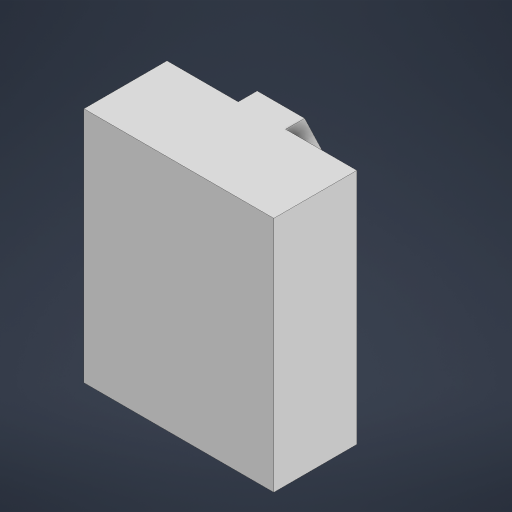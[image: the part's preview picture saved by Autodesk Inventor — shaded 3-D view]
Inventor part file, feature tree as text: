
AUTODESK INVENTOR PART (.ipt)
format: ipt  version: 2024.1 (Build 281209000, 209)  size: 168,960 bytes
history: native  units: mm
features: extrude x3, sketch x3
ambient origin geometry x8: Origin, YZ Plane, XZ Plane, XY Plane, X Axis, Y Axis, Z Axis, Center Point
bodies: Solid1 (feature_tree)
feature tree (6):
  extrude  "Extrusion1"  Depth=3.5mm
  extrude  "Extrusion2"  Depth=2.0mm
  extrude  "Extrusion3"  Depth=3.0mm
  sketch  "Sketch1"  dims[d0=8.0mm d1=3.5mm]
  sketch  "Sketch2"  dims[d2=10.0mm d3=0.0mm d4=2.0mm]
  sketch  "Sketch3"  dims[d5=5.0mm d6=3.0mm d7=3.0mm d8=0.0mm d9=0.8mm d10=0.4mm d11=0.0mm d12=0.0mm]
